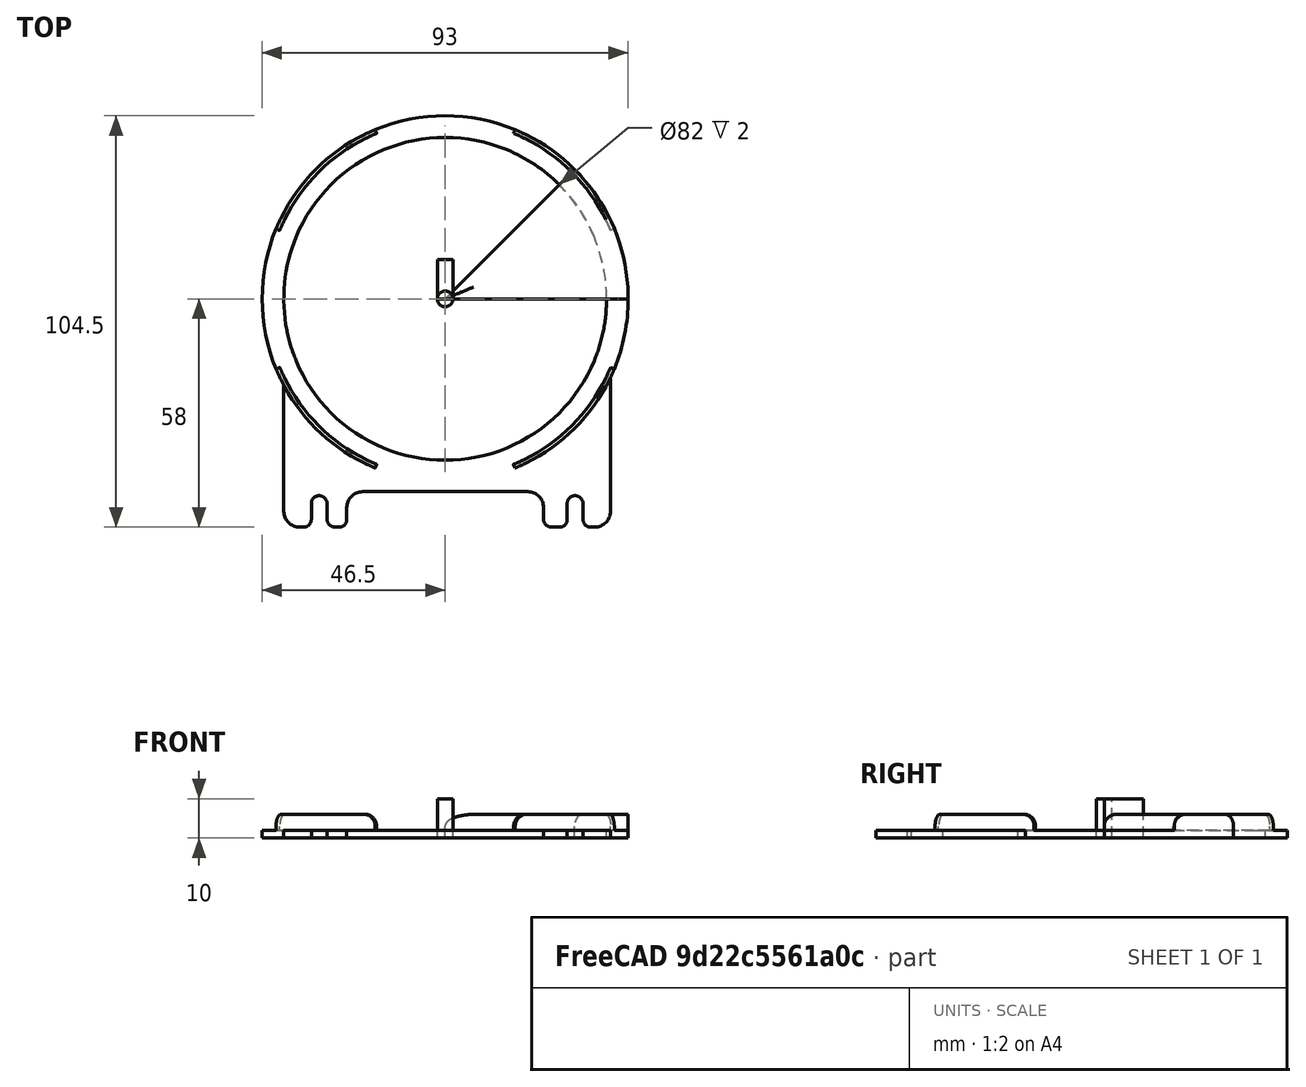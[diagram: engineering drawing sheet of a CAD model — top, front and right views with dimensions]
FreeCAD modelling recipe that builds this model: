
FCSTD DOCUMENT  (FreeCAD 0.19R)
Label: petri_dish_microscope_holder
License: All rights reserved
LicenseURL: http://en.wikipedia.org/wiki/All_rights_reserved
objects: Part::Cylinder×5, Part::MultiFuse×4, Part::Fillet×4, Part::Box×3, Part::FeaturePython×3, Part::Cut×2
note: 18 computed .brp shape members not serialized (recipe doc carries the construction recipe); baked Part::Feature solids carry a one-line shape summary decoded from their .brp

FEATURE [Part::Cylinder] Cylinder  label="outer wall"
  Angle = 45
  AttacherType = Attacher::AttachEngine3D
  Height = 6
  Radius = 46.5
FEATURE [Part::Cylinder] Cylinder001  label="inner cylinder"
  Angle = 360
  AttacherType = Attacher::AttachEngine3D
  Height = 10
  Placement = pos=(0,0,2) rot=(0,0,1;0rad)
  Radius = 45.5
FEATURE [Part::Box] Box  label="Cube"
  AttacherType = Attacher::AttachEngine3D
  Height = 2
  Length = 83
  Placement = pos=(-41,-58,0) rot=(0,0,1;0rad)
  Width = 50
FEATURE [Part::Cylinder] Cylinder002  label="hole cylinder"
  Angle = 360
  AttacherType = Attacher::AttachEngine3D
  Height = 10
  Radius = 41
FEATURE [Part::MultiFuse] Fusion001  label="extract fusion"
  Shapes = -> [Cylinder001,Cylinder002]
FEATURE [Part::Cylinder] Cylinder003  label="bolt hole cylinder"
  Angle = 360
  AttacherType = Attacher::AttachEngine3D
  Height = 10
  Radius = 2
FEATURE [Part::FeaturePython] Array  label="hole array"  # Draft array (typed FeaturePython)
  Angle = 360
  ArrayType = 0
  Axis = (0,0,1)
  Base = -> Cylinder003
  Center = (0,0,0)
  Count = 4
  ExpandArray = false
  Fuse = false
  IntervalAxis = (0,0,0)
  IntervalX = (65,0,0)
  IntervalY = (0,10,0)
  IntervalZ = (0,0,100)
  NumberCircles = 3
  NumberPolar = 5
  NumberX = 2
  NumberY = 2
  NumberZ = 1
  PlacementList = 4 placements: [(0,0,0),(0,10,0),(65,0,0),(65,10,0)]
  RadialDistance = 50
  ScaleList = (4) [(1,1,1),(1,1,1),(1,1,1),(1,1,1)]
  Symmetry = 1
  TangentialDistance = 25
FEATURE [Part::Box] Box001  label="interholde cube"
  AttacherType = Attacher::AttachEngine3D
  Height = 10
  Length = 4
  Placement = pos=(-2,0,0) rot=(0,0,1;0rad)
  Width = 10
FEATURE [Part::FeaturePython] Array001  label="interhole cube array"  # Draft array (typed FeaturePython)
  Angle = 360
  ArrayType = 0
  Axis = (0,0,1)
  Base = -> Box001
  Center = (0,0,0)
  Count = 2
  ExpandArray = false
  Fuse = false
  IntervalAxis = (0,0,0)
  IntervalX = (65,0,0)
  IntervalY = (0,100,0)
  IntervalZ = (0,0,100)
  NumberCircles = 3
  NumberPolar = 5
  NumberX = 2
  NumberY = 1
  NumberZ = 1
  PlacementList = 2 placements: [(-2,0,0),(63,0,0)]
  RadialDistance = 50
  ScaleList = (2) [(1,1,1),(1,1,1)]
  Symmetry = 1
  TangentialDistance = 25
FEATURE [Part::MultiFuse] Fusion002  label="bolt hole fusion"
  Placement = pos=(-32,-62,0) rot=(0,0,1;0rad)
  Shapes = -> [Array001,Array]
FEATURE [Part::Box] Box002  label="Cube001"
  AttacherType = Attacher::AttachEngine3D
  Height = 2
  Length = 50
  Placement = pos=(-25,-58,0) rot=(0,0,1;0rad)
  Width = 9
FEATURE [Part::Fillet] Fillet
  Base = -> Box002
  Edges = 2 edges r=4: [Edge3,Edge7]
FEATURE [Part::Fillet] Fillet001
  Base = -> Box
  Edges = 2 edges r=4: [Edge1,Edge5]
FEATURE [Part::Cylinder] Cylinder004  label="outer cylinder"
  Angle = 360
  AttacherType = Attacher::AttachEngine3D
  Height = 2
  Radius = 46.5
FEATURE [Part::Fillet] Fillet003  label="outer wall fillet"
  Base = -> Cylinder
  Edges = 2 edges r=3: [Edge5,Edge6]
FEATURE [Part::FeaturePython] Array002  label="outer wall array"  # Draft array (typed FeaturePython)
  Angle = 360
  ArrayType = 1
  Axis = (0,0,1)
  Base = -> Fillet003
  Center = (0,0,0)
  Count = 4
  ExpandArray = false
  Fuse = false
  IntervalAxis = (0,0,0)
  IntervalX = (50,0,0)
  IntervalY = (0,50,0)
  IntervalZ = (0,0,50)
  NumberCircles = 3
  NumberPolar = 4
  NumberX = 2
  NumberY = 2
  NumberZ = 1
  Placement = pos=(0,0,0) rot=(0,0,1;0.392699rad)
  PlacementList = 4 placements: [(0,0,0),(0,0,0),(0,0,0),(0,0,0)]
  RadialDistance = 50
  ScaleList = (4) [(1,1,1),(1,1,1),(1,1,1),(1,1,1)]
  Symmetry = 1
  TangentialDistance = 25
FEATURE [Part::MultiFuse] Fusion003
  Shapes = -> [Fusion002,Fillet]
FEATURE [Part::Cut] Cut001
  Base = -> Fillet001
  Tool = -> Fusion003
FEATURE [Part::Fillet] Fillet004
  Base = -> Cut001
  Edges = 6 edges r=2: [Edge47,Edge50,Edge51,Edge56,Edge57,Edge60]
FEATURE [Part::MultiFuse] Fusion
  Shapes = -> [Array002,Cylinder004,Fillet004]
FEATURE [Part::Cut] Cut  label="petri dish microsoft holder"
  Base = -> Fusion
  Tool = -> Fusion001
